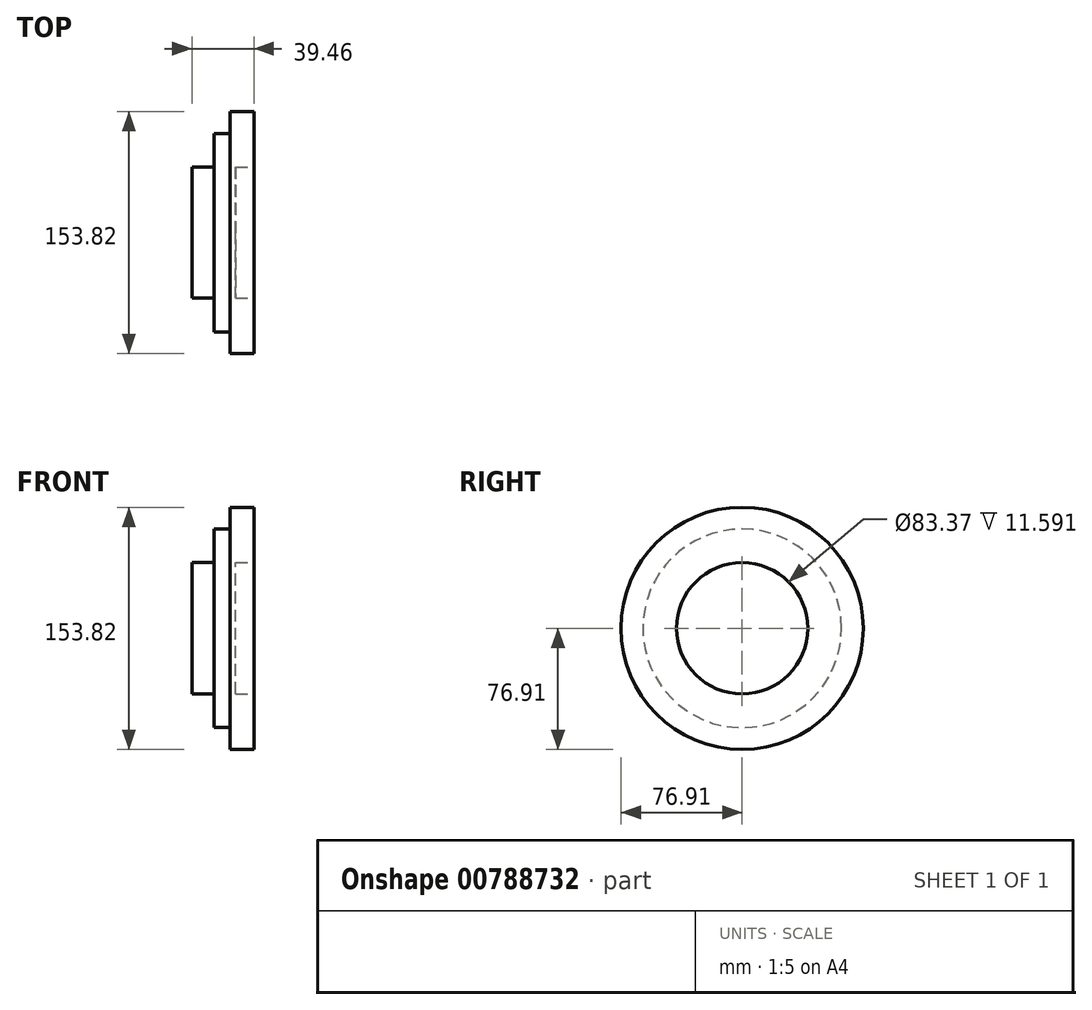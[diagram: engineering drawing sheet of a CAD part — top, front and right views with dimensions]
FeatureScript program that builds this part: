
annotation { "Feature Type Name" : "Feature", "Feature Type Description" : "" }
export const myFeature = defineFeature(function(context is Context, id is Id, definition is map)
    precondition{}
    {
        {
            var Q0;
            Q0=qCreatedBy(makeId("Front.planeOp"),FACE);
            var sketch = newSketch(context, id + "F0", { "sketchPlane" : qUnion([Q0])});
            skLineSegment(sketch, "E0", {"start": v(0, 0) * mm, "end": v(0, 41.68) * mm});
            skLineSegment(sketch, "E1", {"start": v(0, 41.68) * mm, "end": v(14.04, 41.68) * mm});
            skLineSegment(sketch, "E2", {"start": v(14.04, 41.68) * mm, "end": v(14.04, 63.08) * mm});
            skLineSegment(sketch, "E3", {"start": v(14.04, 63.08) * mm, "end": v(24.3, 63.08) * mm});
            skLineSegment(sketch, "E4", {"start": v(24.3, 63.08) * mm, "end": v(24.3, 76.91) * mm});
            skLineSegment(sketch, "E5", {"start": v(24.3, 76.91) * mm, "end": v(39.46, 76.91) * mm});
            skLineSegment(sketch, "E6", {"start": v(39.46, 76.91) * mm, "end": v(39.46, 41.68) * mm});
            skLineSegment(sketch, "E7", {"start": v(39.46, 41.68) * mm, "end": v(27.86, 41.68) * mm});
            skLineSegment(sketch, "E8", {"start": v(27.86, 41.68) * mm, "end": v(27.86, 0) * mm});
            skLineSegment(sketch, "E9", {"start": v(27.86, 0) * mm, "end": v(0, 0) * mm});
            skLineSegment(sketch, "E10", {"start": v(0, 10.03) * mm, "end": v(27.86, 10.03) * mm});
            skSolve(sketch);
        }
        {
            var Q0;
            Q0 = qSketchRegion(id + "F0", true);
            var Q1;
            Q1=sQuery(id+"F0.wireOp",EDGE,"E9");
            revolve(context, id + "F1", {"surfaceOperationType" : NewSurfaceOperationType.NEW, "entities" : qUnion([Q0]), "axis" : qUnion([Q1]), "revolveType" : RevolveType.FULL});
        }
    });
